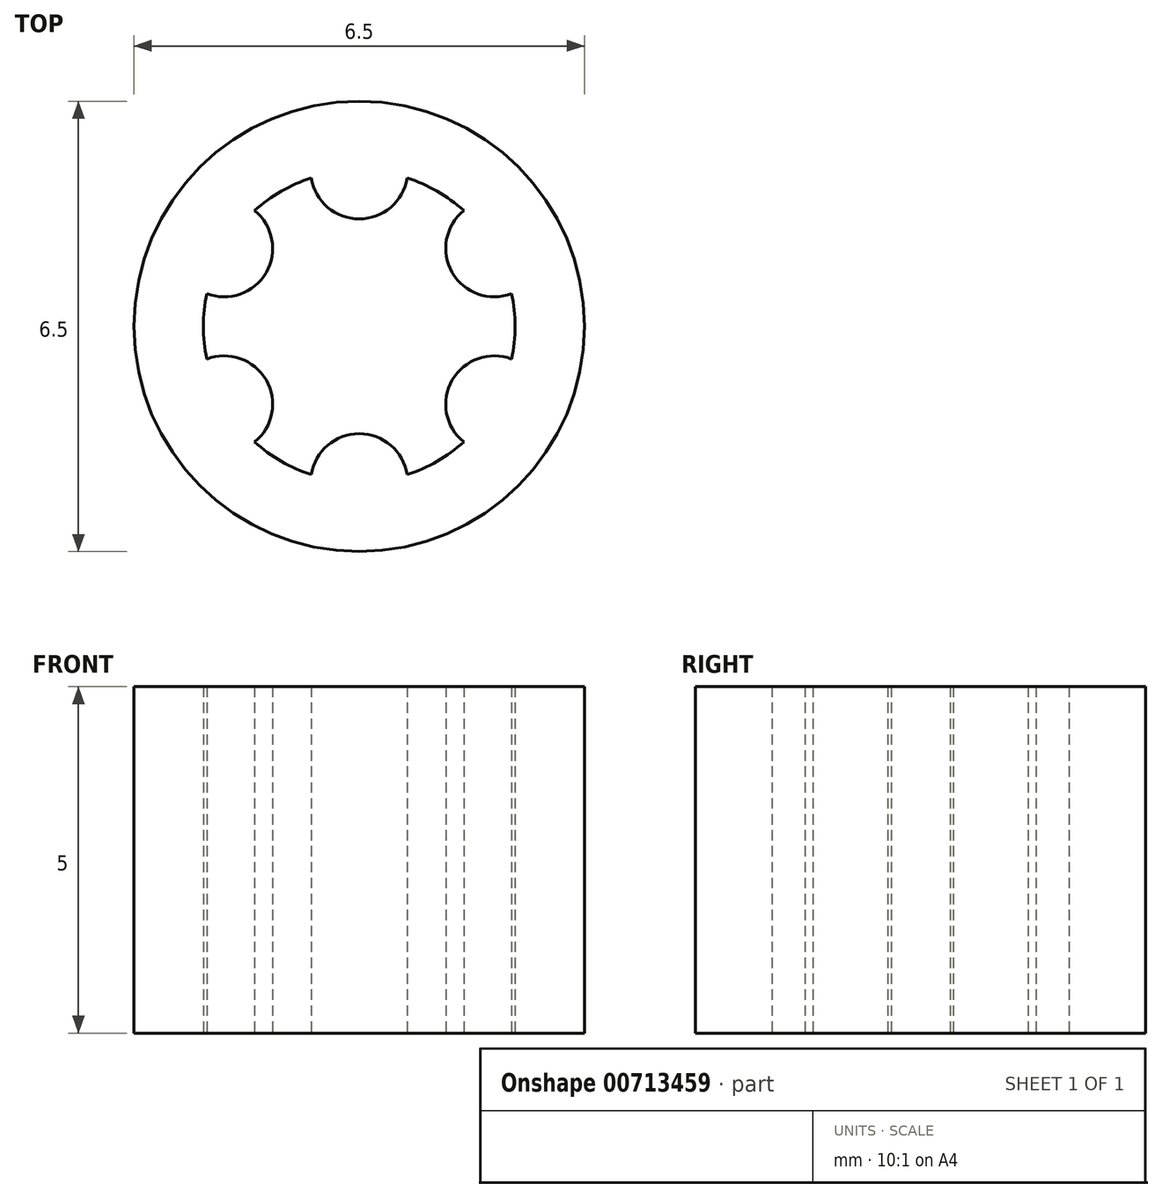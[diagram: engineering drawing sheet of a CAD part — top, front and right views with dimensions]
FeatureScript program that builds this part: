
annotation { "Feature Type Name" : "Feature", "Feature Type Description" : "" }
export const myFeature = defineFeature(function(context is Context, id is Id, definition is map)
    precondition{}
    {
        {
            var Q0;
            Q0=qCreatedBy(makeId("Top.planeOp"),FACE);
            var sketch = newSketch(context, id + "F0", { "sketchPlane" : qUnion([Q0])});
            skCircle(sketch, "E0", {"center": v(0, 0) * mm, "radius": 2.25 * mm});
            skCircle(sketch, "E1", {"center": v(0, 0) * mm, "radius": 3.25 * mm});
            skCircle(sketch, "E2", {"center": v(0, 2.25) * mm, "radius": 0.7 * mm});
            skCircle(sketch, "E3.1.0", {"center": v(-1.95, 1.13) * mm, "radius": 0.7 * mm});
            skCircle(sketch, "E3.2.0", {"center": v(-1.95, -1.12) * mm, "radius": 0.7 * mm});
            skCircle(sketch, "E3.3.0", {"center": v(0, -2.25) * mm, "radius": 0.7 * mm});
            skCircle(sketch, "E3.4.0", {"center": v(1.95, -1.13) * mm, "radius": 0.7 * mm});
            skCircle(sketch, "E3.5.0", {"center": v(1.95, 1.13) * mm, "radius": 0.7 * mm});
            skSolve(sketch);
        }
        {
            var Q0;
            Q0=qSketchRegion(id+"F0",true);
            var Q1;
            {var subQ0=sQuery(id+"F0.wireOp",EDGE,"E3.1.0");var subQ1=sQuery(id+"F0.wireOp",EDGE,"E0");var subQ2=makeQuery(id+"F0.imprint","INTERSECT",VERTEX,{"disambiguationData":[OD(0.0)],"derivedFrom":[subQ1,subQ0]});Q1=makeQuery(id+"F0.imprint","IMPRINT",FACE,{"disambiguationData":[TD([[makeQuery(id+"F0.imprint","IMPRINT",EDGE,{"disambiguationData":[TD([[subQ2,-1.0]])],"derivedFrom":subQ1}),1.0]])]});}
            var Q2;
            {var subQ0=sQuery(id+"F0.wireOp",EDGE,"E3.1.0");var subQ1=sQuery(id+"F0.wireOp",EDGE,"E0");var subQ2=makeQuery(id+"F0.imprint","INTERSECT",VERTEX,{"disambiguationData":[OD(0.0)],"derivedFrom":[subQ1,subQ0]});Q2=makeQuery(id+"F0.imprint","IMPRINT",FACE,{"disambiguationData":[TD([[makeQuery(id+"F0.imprint","IMPRINT",EDGE,{"disambiguationData":[TD([[subQ2,-1.0]])],"derivedFrom":subQ1}),-1.0]])]});}
            var Q3;
            {var subQ0=sQuery(id+"F0.wireOp",EDGE,"E2");var subQ1=sQuery(id+"F0.wireOp",EDGE,"E0");var subQ2=makeQuery(id+"F0.imprint","INTERSECT",VERTEX,{"disambiguationData":[OD(0.0)],"derivedFrom":[subQ1,subQ0]});Q3=makeQuery(id+"F0.imprint","IMPRINT",FACE,{"disambiguationData":[TD([[makeQuery(id+"F0.imprint","IMPRINT",EDGE,{"disambiguationData":[TD([[subQ2,-1.0]])],"derivedFrom":subQ1}),-1.0]])]});}
            var Q4;
            {var subQ0=sQuery(id+"F0.wireOp",EDGE,"E2");var subQ1=sQuery(id+"F0.wireOp",EDGE,"E0");var subQ2=makeQuery(id+"F0.imprint","INTERSECT",VERTEX,{"disambiguationData":[OD(0.0)],"derivedFrom":[subQ1,subQ0]});Q4=makeQuery(id+"F0.imprint","IMPRINT",FACE,{"disambiguationData":[TD([[makeQuery(id+"F0.imprint","IMPRINT",EDGE,{"disambiguationData":[TD([[subQ2,-1.0]])],"derivedFrom":subQ1}),1.0]])]});}
            var Q5;
            {var subQ0=sQuery(id+"F0.wireOp",EDGE,"E3.5.0");var subQ1=sQuery(id+"F0.wireOp",EDGE,"E0");var subQ2=makeQuery(id+"F0.imprint","INTERSECT",VERTEX,{"disambiguationData":[OD(0.0)],"derivedFrom":[subQ1,subQ0]});Q5=makeQuery(id+"F0.imprint","IMPRINT",FACE,{"disambiguationData":[TD([[makeQuery(id+"F0.imprint","IMPRINT",EDGE,{"disambiguationData":[TD([[subQ2,1.0]])],"derivedFrom":subQ1}),-1.0]])]});}
            var Q6;
            {var subQ0=sQuery(id+"F0.wireOp",EDGE,"E3.5.0");var subQ1=sQuery(id+"F0.wireOp",EDGE,"E0");var subQ2=makeQuery(id+"F0.imprint","INTERSECT",VERTEX,{"disambiguationData":[OD(0.0)],"derivedFrom":[subQ1,subQ0]});Q6=makeQuery(id+"F0.imprint","IMPRINT",FACE,{"disambiguationData":[TD([[makeQuery(id+"F0.imprint","IMPRINT",EDGE,{"disambiguationData":[TD([[subQ2,1.0]])],"derivedFrom":subQ1}),1.0]])]});}
            var Q7;
            {var subQ0=sQuery(id+"F0.wireOp",EDGE,"E3.4.0");var subQ1=sQuery(id+"F0.wireOp",EDGE,"E0");var subQ2=makeQuery(id+"F0.imprint","INTERSECT",VERTEX,{"disambiguationData":[OD(0.0)],"derivedFrom":[subQ1,subQ0]});Q7=makeQuery(id+"F0.imprint","IMPRINT",FACE,{"disambiguationData":[TD([[makeQuery(id+"F0.imprint","IMPRINT",EDGE,{"disambiguationData":[TD([[subQ2,-1.0]])],"derivedFrom":subQ1}),-1.0]])]});}
            var Q8;
            {var subQ0=sQuery(id+"F0.wireOp",EDGE,"E3.3.0");var subQ1=sQuery(id+"F0.wireOp",EDGE,"E0");var subQ2=makeQuery(id+"F0.imprint","INTERSECT",VERTEX,{"disambiguationData":[OD(0.0)],"derivedFrom":[subQ1,subQ0]});Q8=makeQuery(id+"F0.imprint","IMPRINT",FACE,{"disambiguationData":[TD([[makeQuery(id+"F0.imprint","IMPRINT",EDGE,{"disambiguationData":[TD([[subQ2,-1.0]])],"derivedFrom":subQ1}),-1.0]])]});}
            var Q9;
            {var subQ0=sQuery(id+"F0.wireOp",EDGE,"E3.2.0");var subQ1=sQuery(id+"F0.wireOp",EDGE,"E0");var subQ2=makeQuery(id+"F0.imprint","INTERSECT",VERTEX,{"disambiguationData":[OD(0.0)],"derivedFrom":[subQ1,subQ0]});Q9=makeQuery(id+"F0.imprint","IMPRINT",FACE,{"disambiguationData":[TD([[makeQuery(id+"F0.imprint","IMPRINT",EDGE,{"disambiguationData":[TD([[subQ2,-1.0]])],"derivedFrom":subQ1}),-1.0]])]});}
            var Q10;
            {var subQ0=sQuery(id+"F0.wireOp",EDGE,"E3.3.0");var subQ1=sQuery(id+"F0.wireOp",EDGE,"E0");var subQ2=makeQuery(id+"F0.imprint","INTERSECT",VERTEX,{"disambiguationData":[OD(0.0)],"derivedFrom":[subQ1,subQ0]});Q10=makeQuery(id+"F0.imprint","IMPRINT",FACE,{"disambiguationData":[TD([[makeQuery(id+"F0.imprint","IMPRINT",EDGE,{"disambiguationData":[TD([[subQ2,-1.0]])],"derivedFrom":subQ1}),1.0]])]});}
            var Q11;
            {var subQ0=sQuery(id+"F0.wireOp",EDGE,"E3.2.0");var subQ1=sQuery(id+"F0.wireOp",EDGE,"E0");var subQ2=makeQuery(id+"F0.imprint","INTERSECT",VERTEX,{"disambiguationData":[OD(0.0)],"derivedFrom":[subQ1,subQ0]});Q11=makeQuery(id+"F0.imprint","IMPRINT",FACE,{"disambiguationData":[TD([[makeQuery(id+"F0.imprint","IMPRINT",EDGE,{"disambiguationData":[TD([[subQ2,-1.0]])],"derivedFrom":subQ1}),1.0]])]});}
            var Q12;
            {var subQ0=sQuery(id+"F0.wireOp",EDGE,"E3.4.0");var subQ1=sQuery(id+"F0.wireOp",EDGE,"E0");var subQ2=makeQuery(id+"F0.imprint","INTERSECT",VERTEX,{"disambiguationData":[OD(0.0)],"derivedFrom":[subQ1,subQ0]});Q12=makeQuery(id+"F0.imprint","IMPRINT",FACE,{"disambiguationData":[TD([[makeQuery(id+"F0.imprint","IMPRINT",EDGE,{"disambiguationData":[TD([[subQ2,-1.0]])],"derivedFrom":subQ1}),1.0]])]});}
            extrude(context, id + "F1", {"entities" : qUnion([Q0, Q1, Q2, Q3, Q4, Q5, Q6, Q7, Q8, Q9, Q10, Q11, Q12]), "depth" : 5 * mm, "offsetDistance" : 25 * mm});
        }
    });
